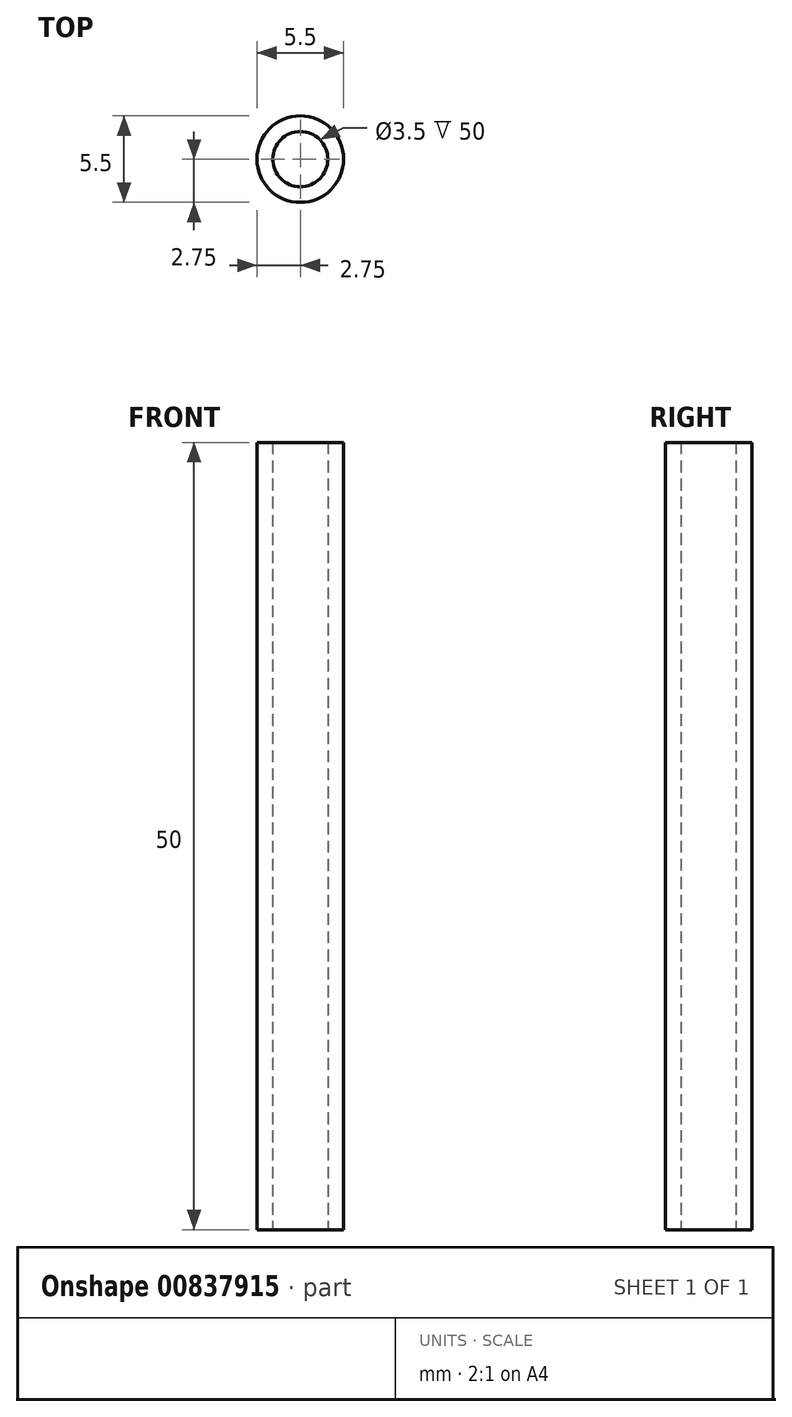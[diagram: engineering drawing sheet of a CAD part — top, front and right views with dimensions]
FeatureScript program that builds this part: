
annotation { "Feature Type Name" : "Feature", "Feature Type Description" : "" }
export const myFeature = defineFeature(function(context is Context, id is Id, definition is map)
    precondition{}
    {
        {
            var Q0;
            Q0=qCreatedBy(makeId("Top.planeOp"),FACE);
            var sketch = newSketch(context, id + "F0", { "sketchPlane" : qUnion([Q0])});
            skCircle(sketch, "E0", {"center": v(0, 0) * mm, "radius": 2.75 * mm});
            skSolve(sketch);
        }
        {
            var Q0;
            Q0=makeQuery(id+"F0.imprint","IMPRINT",FACE,{"disambiguationData":[TD([[makeQuery(id+"F0.imprint","IMPRINT",EDGE,{"derivedFrom":sQuery(id+"F0.wireOp",EDGE,"E0")}),1.0]])]});
            var sketch = newSketch(context, id + "F1", { "sketchPlane" : qUnion([Q0])});
            skCircle(sketch, "E1", {"center": v(0, 0) * mm, "radius": 1.75 * mm});
            skSolve(sketch);
        }
        {
            var Q0;
            Q0 = qSketchRegion(id + "F0", true);
            extrude(context, id + "F2", {"entities" : qUnion([Q0]), "depth" : 50 * mm, "offsetDistance" : 25 * mm});
        }
        {
            var Q0;
            Q0 = qSketchRegion(id + "F1", true);
            extrude(context, id + "F3", {"entities" : qUnion([Q0]), "operationType" : NewBodyOperationType.REMOVE, "depth" : 50 * mm, "offsetDistance" : 25 * mm});
        }
    });
